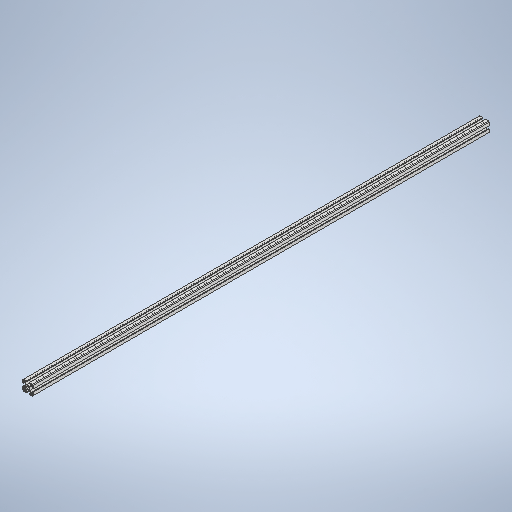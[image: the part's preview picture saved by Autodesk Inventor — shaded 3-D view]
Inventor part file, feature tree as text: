
AUTODESK INVENTOR PART (.ipt)
format: ipt  version: 2025 (Build 290162000, 162)  size: 315,392 bytes
history: native  units: in
note: dims shown in document units (in); Inventor stores cm internally (conversion verified against a paired STEP export)
features: extrude x1, sketch x1
ambient origin geometry x8: Origin, YZ Plane, XZ Plane, XY Plane, X Axis, Y Axis, Z Axis, Center Point
bodies: Solid1 (feature_tree)
feature tree (2):
  extrude  "Extrusion1"  Depth=52.7559in
  sketch  "Sketch1"  dims[d6=52.7559in d7=0.0in d8=0.1969in d9=0.0344in]
